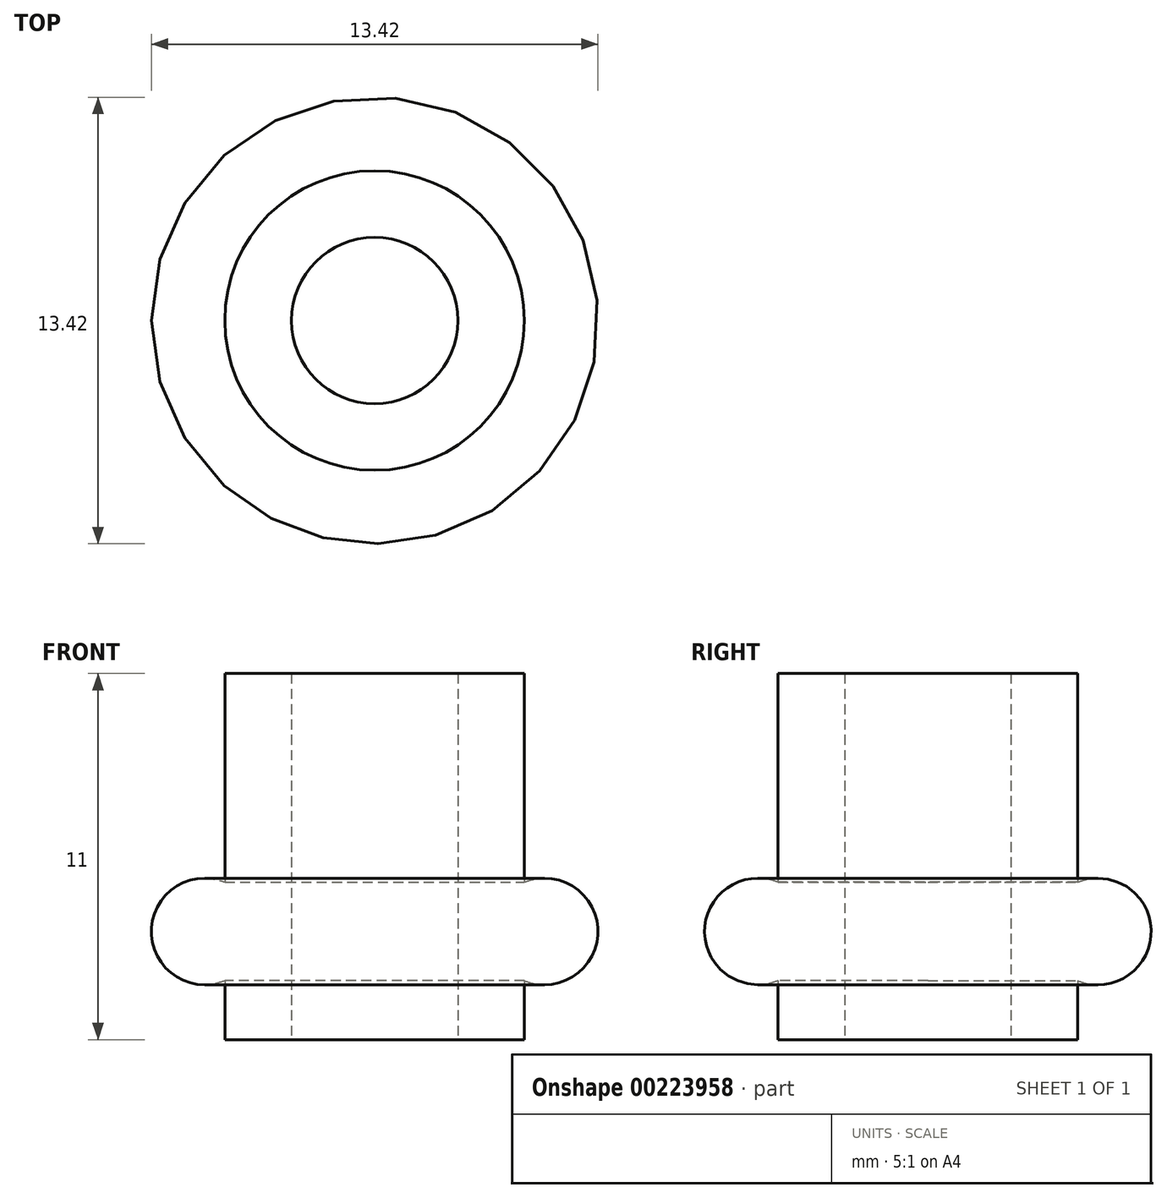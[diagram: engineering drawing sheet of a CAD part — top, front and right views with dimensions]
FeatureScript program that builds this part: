
annotation { "Feature Type Name" : "Feature", "Feature Type Description" : "" }
export const myFeature = defineFeature(function(context is Context, id is Id, definition is map)
    precondition{}
    {
        {
            var Q0;
            Q0=qCreatedBy(makeId("Front.planeOp"),FACE);
            var sketch = newSketch(context, id + "F3", { "sketchPlane" : qUnion([Q0])});
            skLineSegment(sketch, "E0.bottom", {"start": v(2.5, 0) * mm, "end": v(4.5, 0) * mm});
            skLineSegment(sketch, "E0.top", {"start": v(2.5, 11) * mm, "end": v(4.5, 11) * mm});
            skLineSegment(sketch, "E0.left", {"start": v(2.5, 0) * mm, "end": v(2.5, 11) * mm});
            skLineSegment(sketch, "E0.right", {"start": v(4.5, 0) * mm, "end": v(4.5, 11) * mm});
            skLineSegment(sketch, "E1", {"start": v(0, 0) * mm, "end": v(0, 143.6) * mm});
            skSolve(sketch);
        }
        {
            var Q0;
            Q0=makeQuery(id+"F3.imprint","IMPRINT",FACE,{"disambiguationData":[TD([[makeQuery(id+"F3.imprint","IMPRINT",EDGE,{"derivedFrom":sQuery(id+"F3.wireOp",EDGE,"E0.bottom")}),1.0]])]});
            var Q1;
            Q1=sQuery(id+"F3.wireOp",EDGE,"E1");
            revolve(context, id + "F0", {"entities" : qUnion([Q0]), "axis" : qUnion([Q1]), "revolveType" : RevolveType.FULL});
        }
        {
            var Q0;
            Q0=qCreatedBy(makeId("Front.planeOp"),FACE);
            var sketch = newSketch(context, id + "F1", { "sketchPlane" : qUnion([Q0])});
            skCircle(sketch, "E2", {"center": v(5.11, 3.25) * mm, "radius": 1.6 * mm});
            skLineSegment(sketch, "E3", {"start": v(3.5, -45.34) * mm, "end": v(3.5, 293.02) * mm, "construction": true});
            skSolve(sketch);
        }
        {
            var Q0;
            Q0 = qSketchRegion(id + "F1", true);
            var Q1;
            Q1=makeQuery(id+"F0.opRevolve","SWEPT_FACE",FACE,{"disambiguationData":[OSD([sQuery(id+"F3.wireOp",EDGE,"E0.right")])]});
            revolve(context, id + "F2", {"operationType" : NewBodyOperationType.ADD, "entities" : qUnion([Q0]), "axis" : qUnion([Q1]), "revolveType" : RevolveType.FULL});
        }
    });
